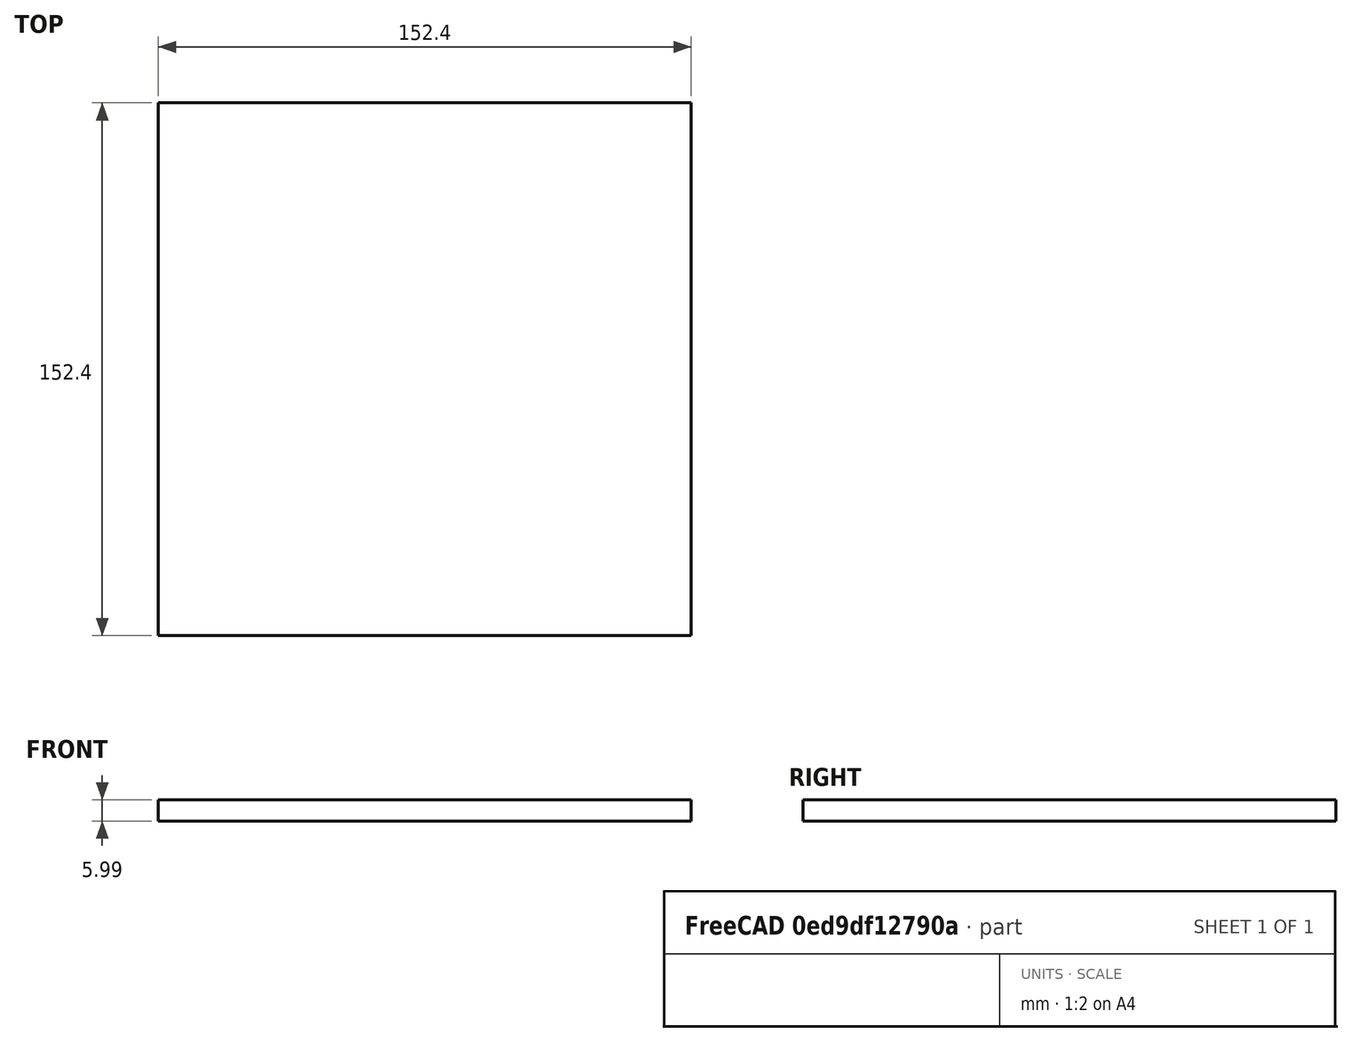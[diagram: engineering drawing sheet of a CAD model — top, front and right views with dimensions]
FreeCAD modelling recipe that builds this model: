
FCSTD DOCUMENT  (FreeCAD 0.19R24267 (Git))
Label: Up1-P12
License: All rights reserved
LicenseURL: http://en.wikipedia.org/wiki/All_rights_reserved
objects: TechDraw::DrawViewDimension×3, TechDraw::DrawProjGroupItem×2, TechDraw::DrawHatch×2, TechDraw::DrawViewAnnotation×2, Sketcher::SketchObject×1, Part::Extrusion×1, TechDraw::DrawSVGTemplate×1, TechDraw::DrawProjGroup×1, TechDraw::DrawPage×1
note: 2 computed .brp shape members not serialized (recipe doc carries the construction recipe); baked Part::Feature solids carry a one-line shape summary decoded from their .brp

FEATURE [Sketcher::SketchObject] Sketch
  FullyConstrained = false
  sketch-geometry (4):
    g0: LineSegment StartX=-49.9746 StartY=98.2281 StartZ=0 EndX=102.425 EndY=98.2281 EndZ=0
    g1: LineSegment StartX=102.425 StartY=98.2281 StartZ=0 EndX=102.425 EndY=-54.1719 EndZ=0
    g2: LineSegment StartX=102.425 StartY=-54.1719 StartZ=0 EndX=-49.9746 EndY=-54.1719 EndZ=0
    g3: LineSegment StartX=-49.9746 StartY=-54.1719 StartZ=0 EndX=-49.9746 EndY=98.2281 EndZ=0
  constraints (10):
    c: Coincident(g0,g1)
    c: Coincident(g1,g2)
    c: Coincident(g2,g3)
    c: Coincident(g3,g0)
    c: Horizontal(g0)
    c: Horizontal(g2)
    c: Vertical(g1)
    c: Vertical(g3)
    c: DistanceY(g3,g3) = 152.4
    c: DistanceX(g0,g0) = 152.4
FEATURE [Part::Extrusion] Extrude
  Base = -> Sketch
  Dir = (0,0,1)
  DirMode = 2
  FaceMakerClass = Part::FaceMakerBullseye
  LengthFwd = 5.9944
  LengthRev = 0
  Solid = true
  Symmetric = false
FEATURE [TechDraw::DrawSVGTemplate] Template
  Height = 215.9
  Orientation = 1
  Width = 279.4
FEATURE [TechDraw::DrawProjGroupItem] ProjItem  label="Front"
  CoarseView = false
  Direction = (0,0,1)
  Focus = 100
  HardHidden = false
  IsoCount = 0
  IsoHidden = false
  IsoVisible = false
  LockPosition = true
  Perspective = false
  Rotation = 0
  RotationVector = (-1,0,0)
  Scale = 0.25
  ScaleType = 2
  SeamHidden = false
  SeamVisible = true
  SmoothHidden = false
  SmoothVisible = true
  Source = -> [Extrude]
  Type = 0
  X = 0
  XDirection = (-1,0,0)
  Y = 0
FEATURE [TechDraw::DrawProjGroupItem] ProjItem001  label="Left"
  CoarseView = false
  Direction = (1,0,1e-16)
  Focus = 100
  HardHidden = false
  IsoCount = 0
  IsoHidden = false
  IsoVisible = false
  LockPosition = false
  Perspective = false
  Rotation = 0
  RotationVector = (1,0,0)
  Scale = 0.25
  ScaleType = 2
  SeamHidden = false
  SeamVisible = true
  SmoothHidden = false
  SmoothVisible = true
  Source = -> [Extrude]
  Type = 1
  X = 46.9171
  XDirection = (-1e-16,0,1)
  Y = 0
FEATURE [TechDraw::DrawProjGroup] ProjGroup
  Anchor = -> ProjItem
  AutoDistribute = true
  LockPosition = false
  ProjectionType = 0
  Rotation = 0
  Scale = 0.25
  ScaleType = 2
  Source = -> [Extrude]
  Views = -> [ProjItem,ProjItem001]
  X = 124.47
  Y = 106.338
  spacingX = 15.0114
  spacingY = 15.0114
FEATURE [TechDraw::DrawHatch] Hatch  label="HatchF0"
  HatchPattern = <path>
  Source = -> ProjItem [Face0]
FEATURE [TechDraw::DrawHatch] Hatch001  label="Hatch001F0"
  HatchPattern = <path>
  Source = -> ProjItem001 [Face0]
FEATURE [TechDraw::DrawViewDimension] Dimension
  Arbitrary = false
  ArbitraryTolerances = false
  EqualTolerance = true
  FormatSpec = %.3f
  FormatSpecOverTolerance = %+.3f
  FormatSpecUnderTolerance = %+.3f
  Inverted = false
  LockPosition = false
  MeasureType = 1
  OverTolerance = 0
  References2D = -> [ProjItem]
  Rotation = 0
  ScaleType = 0
  TheoreticalExact = false
  Type = 1
  UnderTolerance = 0
  X = 0.306502
  Y = 33.1491
FEATURE [TechDraw::DrawViewDimension] Dimension001
  Arbitrary = false
  ArbitraryTolerances = false
  EqualTolerance = true
  FormatSpec = %.3f
  FormatSpecOverTolerance = %+.3f
  FormatSpecUnderTolerance = %+.3f
  Inverted = false
  LockPosition = false
  MeasureType = 1
  OverTolerance = 0
  References2D = -> [ProjItem]
  Rotation = 0
  ScaleType = 0
  TheoreticalExact = false
  Type = 2
  UnderTolerance = 0
  X = 22.9522
  Y = 2.12849
FEATURE [TechDraw::DrawViewDimension] Dimension002
  Arbitrary = false
  ArbitraryTolerances = false
  EqualTolerance = true
  FormatSpec = %.3f
  FormatSpecOverTolerance = %+.3f
  FormatSpecUnderTolerance = %+.3f
  Inverted = false
  LockPosition = false
  MeasureType = 1
  OverTolerance = 0
  References2D = -> [ProjItem001]
  Rotation = 0
  ScaleType = 0
  TheoreticalExact = false
  Type = 1
  UnderTolerance = 0
  X = 16.338
  Y = 11.6936
FEATURE [TechDraw::DrawViewAnnotation] Annotation
  Font = osifont
  LineSpace = 80
  LockPosition = false
  MaxWidth = -1
  Rotation = 0
  ScaleType = 0
  Text = Figure S3 (Upright) | Panel 12 [door] | Quantity: 2
  TextSize = 5.0038
  TextStyle = 0
  X = 29.5622
  Y = 195.58
FEATURE [TechDraw::DrawViewAnnotation] Annotation002
  Font = osifont
  LineSpace = 80
  LockPosition = false
  MaxWidth = -1
  Rotation = 0
  ScaleType = 0
  Text = Units: Inches
  TextSize = 5.0038
  TextStyle = 0
  X = 259.08
  Y = 5.08
FEATURE [TechDraw::DrawPage] Page
  KeepUpdated = true
  NextBalloonIndex = 1
  ProjectionType = 0
  Template = -> Template
  Views = -> [ProjGroup,Dimension,Dimension001,Dimension002,Annotation,Annotation002]
note: 2 file-system paths scrubbed to <path> (originals preserved in the JSON sidecar)
